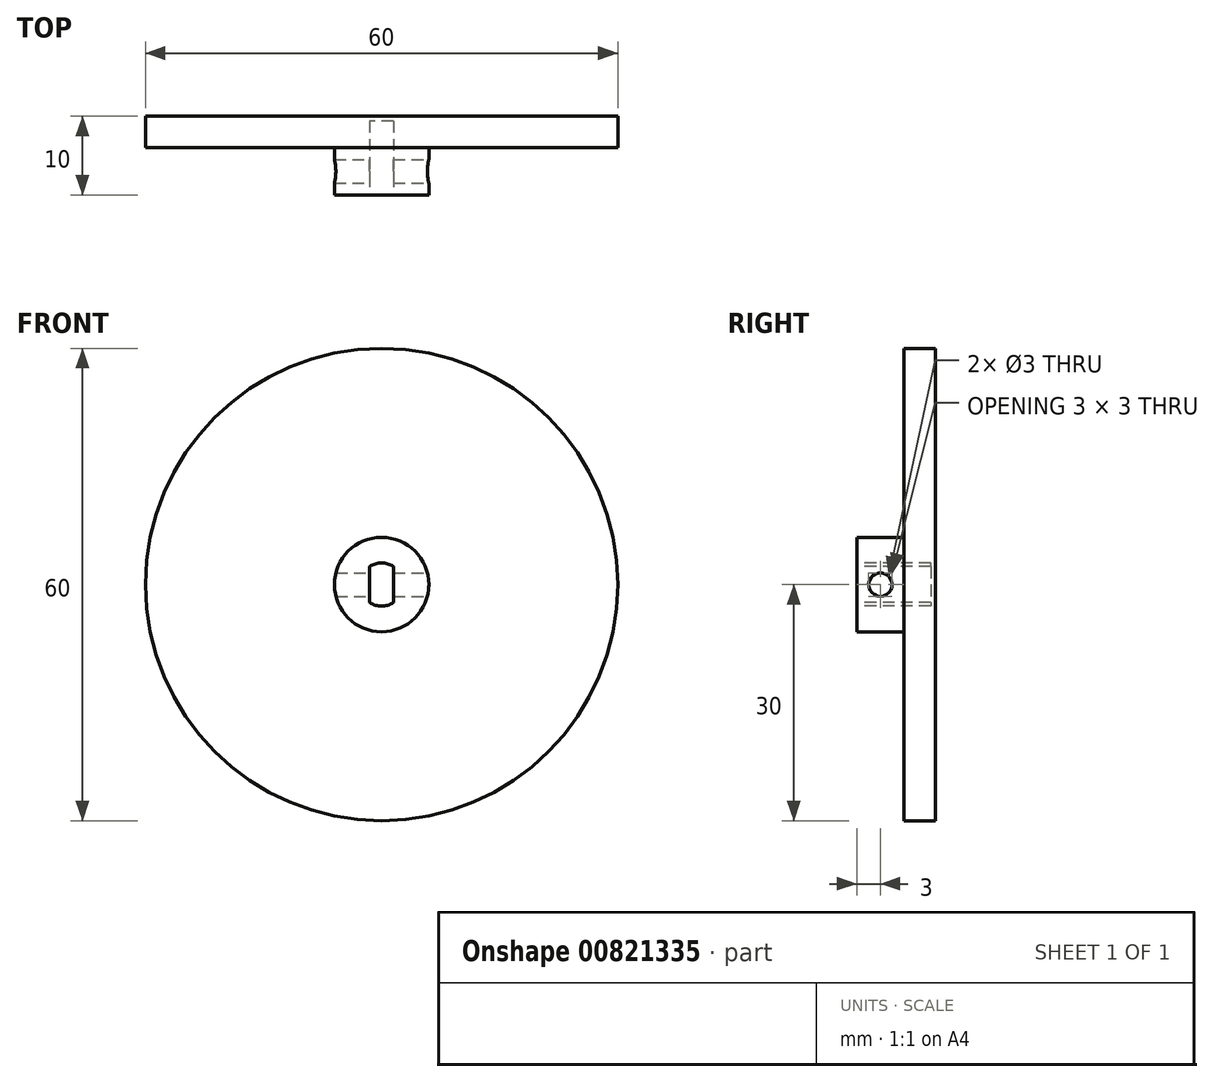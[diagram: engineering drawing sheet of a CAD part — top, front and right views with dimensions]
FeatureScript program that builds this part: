
annotation { "Feature Type Name" : "Feature", "Feature Type Description" : "" }
export const myFeature = defineFeature(function(context is Context, id is Id, definition is map)
    precondition{}
    {
        {
            var Q0;
            Q0=qCreatedBy(makeId("Front.planeOp"),FACE);
            var sketch = newSketch(context, id + "F0", { "sketchPlane" : qUnion([Q0])});
            skCircle(sketch, "E0", {"center": v(0, 0) * mm, "radius": 30 * mm});
            skCircle(sketch, "E1", {"center": v(0, 0) * mm, "radius": 6 * mm});
            skSolve(sketch);
        }
        {
            var Q0;
            Q0=makeQuery(id+"F0.imprint","IMPRINT",FACE,{"disambiguationData":[TD([[makeQuery(id+"F0.imprint","IMPRINT",EDGE,{"derivedFrom":sQuery(id+"F0.wireOp",EDGE,"E1")}),1.0]])]});
            var Q1;
            Q1=makeQuery(id+"F0.imprint","IMPRINT",FACE,{"disambiguationData":[TD([[makeQuery(id+"F0.imprint","IMPRINT",EDGE,{"derivedFrom":sQuery(id+"F0.wireOp",EDGE,"E0")}),1.0]])]});
            extrude(context, id + "F1", {"entities" : qUnion([Q0, Q1]), "oppositeDirection" : true, "depth" : 4 * mm, "offsetDistance" : 25 * mm});
        }
        {
            var Q0;
            Q0=makeQuery(id+"F0.imprint","IMPRINT",FACE,{"disambiguationData":[TD([[makeQuery(id+"F0.imprint","IMPRINT",EDGE,{"derivedFrom":sQuery(id+"F0.wireOp",EDGE,"E1")}),1.0]])]});
            extrude(context, id + "F2", {"entities" : qUnion([Q0]), "operationType" : NewBodyOperationType.ADD, "depth" : 6 * mm, "offsetDistance" : 25 * mm});
        }
        {
            var Q0;
            Q0=qCreatedBy(makeId("Right.planeOp"),FACE);
            var sketch = newSketch(context, id + "F3", { "sketchPlane" : qUnion([Q0])});
            skCircle(sketch, "E2", {"center": v(-3, 0) * mm, "radius": 1.5 * mm});
            skSolve(sketch);
        }
        {
            var Q0;
            Q0 = qSketchRegion(id + "F3", true);
            extrude(context, id + "F4", {"entities" : qUnion([Q0]), "operationType" : NewBodyOperationType.REMOVE, "endBound" : BoundingType.SYMMETRIC, "oppositeDirection" : true, "depth" : 25 * mm, "offsetDistance" : 25 * mm});
        }
        {
            var Q0;
            Q0=makeQuery(id+"F2.opExtrude","CAP_FACE",FACE,{"disambiguationData":[OSD([sQuery(id+"F0.wireOp",EDGE,"E1")])],"isStart":false});
            var sketch = newSketch(context, id + "F5", { "sketchPlane" : qUnion([Q0])});
            skLineSegment(sketch, "E3.bottom", {"start": v(1.5, 2.3) * mm, "end": v(-1.5, 2.3) * mm});
            skLineSegment(sketch, "E3.top", {"start": v(1.5, -2.3) * mm, "end": v(-1.5, -2.3) * mm});
            skLineSegment(sketch, "E3.left", {"start": v(1.5, 2.3) * mm, "end": v(1.5, -2.3) * mm});
            skLineSegment(sketch, "E3.right", {"start": v(-1.5, 2.3) * mm, "end": v(-1.5, -2.3) * mm});
            skPoint(sketch, "E3.middle", {"position": v(0, 0) * mm});
            skArc(sketch, "E4", {"start": v(1.5, 2.3) * mm, "mid": v(0, 2.75) * mm, "end": v(-1.5, 2.3) * mm});
            skArc(sketch, "E5", {"start": v(-1.5, -2.3) * mm, "mid": v(0, -2.75) * mm, "end": v(1.5, -2.3) * mm});
            skSolve(sketch);
        }
        {
            var Q0;
            Q0 = qSketchRegion(id + "F5", true);
            extrude(context, id + "F6", {"entities" : qUnion([Q0]), "operationType" : NewBodyOperationType.REMOVE, "oppositeDirection" : true, "depth" : 9.4 * mm, "offsetDistance" : 25 * mm});
        }
    });
